# Revit family: 201_RINO-_
name_source: partatom
category: Air Terminals
units: mm (PartAtom-declared; Revit-internal decimal feet)

## family parameters
Always vertical = Yes
Cut with Voids When Loaded = No
Part Type = Normal
Room Calculation Point = Yes
Round Connector Dimension = Use Diameter
Shared = No
Work Plane-Based = No

## types (3) — shared parameters
CL_Location_5000 = 5000 mm  [stored 16.4042 ft]
COL1 = Yes
COL2 = No
COL3 = No
Description = Air diffuser
L_ARR = 400 mm  [stored 1.31234 ft]
Manufacturer = Climecon
QmdConnectorList = 201;D
URL = www.climecon.fi
W_ARR = 400 mm  [stored 1.31234 ft]
magiPartTypeId = 201
magiProductFamilyId = RINO-*
zero-valued in all types: CLBTZ, H_ARR

## per-type parameters (varying)
| type | A | C | D |
| RINO-100 | 206 mm | 21 mm | 100 mm |
| RINO-125 | 206 mm | 30 mm  [stored 0.0984252 ft] | 125 mm |
| RINO-160 | 246 mm  [stored 0.807087 ft] | 39 mm  [stored 0.127953 ft] | 160 mm |

note: column(s) folded — value = type name in every type: MC Product Code, magiProductId

note: [stored X ft] marks values corroborated as IEEE doubles in the binary element streams (Revit-internal decimal feet)

## geometry (parser evidence)
native form markers: Sweep x1
no freeform markers — native parametric forms only
